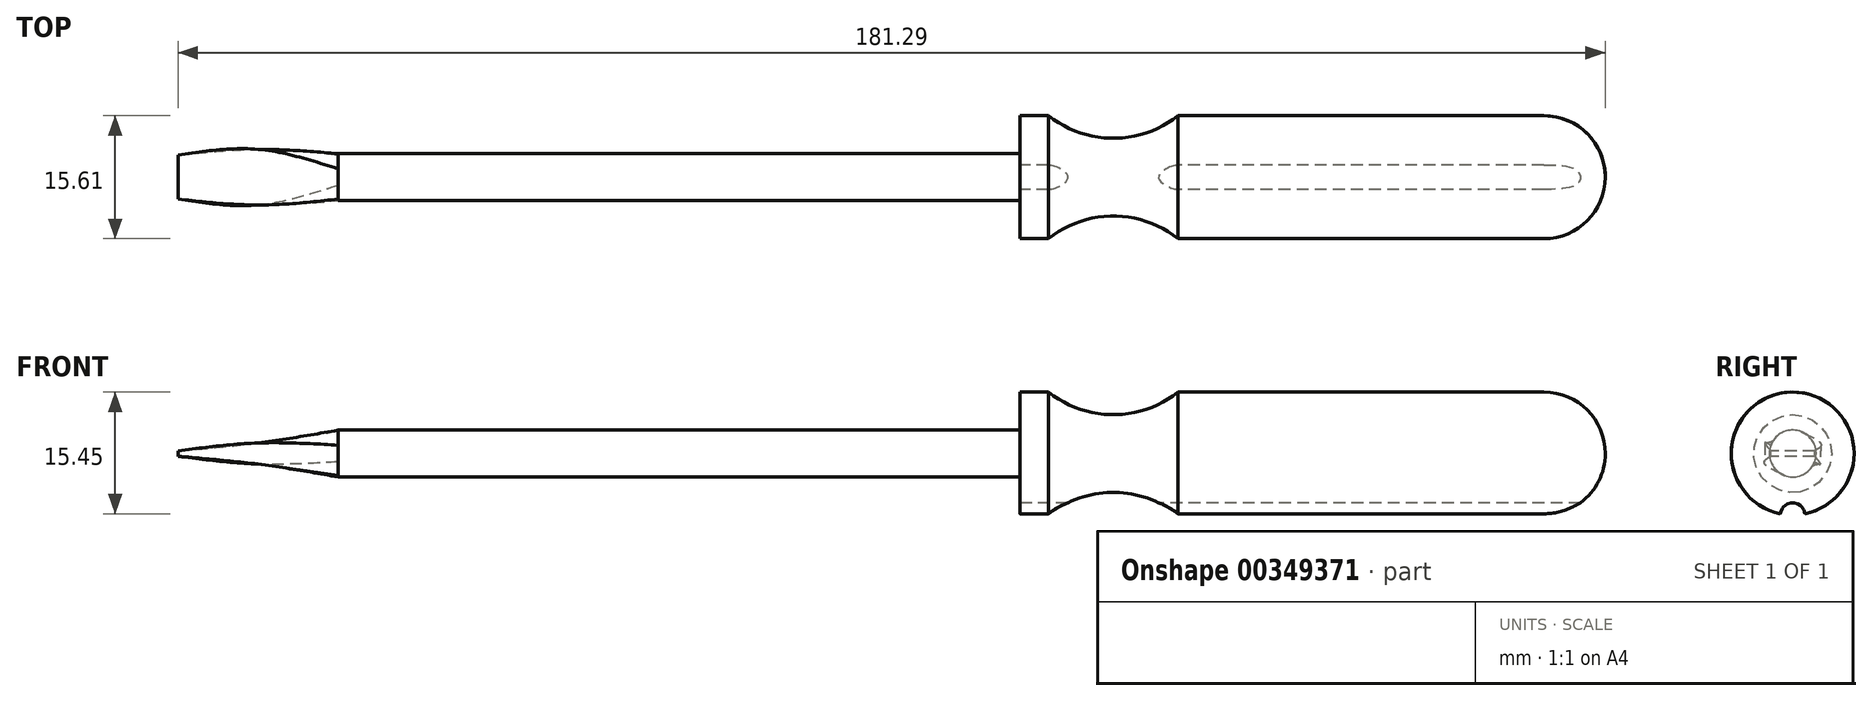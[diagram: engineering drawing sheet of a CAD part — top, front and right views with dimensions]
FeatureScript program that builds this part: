
annotation { "Feature Type Name" : "Feature", "Feature Type Description" : "" }
export const myFeature = defineFeature(function(context is Context, id is Id, definition is map)
    precondition{}
    {
        {
            var Q0;
            Q0=qCreatedBy(makeId("Top.planeOp"),FACE);
            var sketch = newSketch(context, id + "F0", { "sketchPlane" : qUnion([Q0])});
            skLineSegment(sketch, "E0", {"start": v(0, 0) * mm, "end": v(-46.47, 0) * mm});
            skLineSegment(sketch, "E1", {"start": v(0, 0) * mm, "end": v(0, -7.8) * mm, "construction": true});
            skArc(sketch, "E2", {"start": v(0, 0) * mm, "mid": v(5.52, -2.29) * mm, "end": v(7.8, -7.8) * mm});
            skLineSegment(sketch, "E3", {"start": v(7.8, -7.8) * mm, "end": v(-66.56, -7.8) * mm});
            skLineSegment(sketch, "E4", {"start": v(-66.56, -7.8) * mm, "end": v(-66.56, 0) * mm});
            skLineSegment(sketch, "E5", {"start": v(-66.56, 0) * mm, "end": v(-62.92, 0) * mm});
            skArc(sketch, "E6", {"start": v(-62.92, 0) * mm, "mid": v(-54.7, -2.86) * mm, "end": v(-46.47, 0) * mm});
            skSolve(sketch);
        }
        {
            var Q0;
            Q0=makeQuery(id+"F0.imprint","IMPRINT",FACE,{"disambiguationData":[TD([[makeQuery(id+"F0.imprint","IMPRINT",EDGE,{"derivedFrom":sQuery(id+"F0.wireOp",EDGE,"E0")}),1.0]])]});
            var Q1;
            Q1=sQuery(id+"F0.wireOp",EDGE,"E3");
            revolve(context, id + "F1", {"entities" : qUnion([Q0]), "axis" : qUnion([Q1]), "revolveType" : RevolveType.FULL});
        }
        {
            var Q0;
            Q0=makeQuery(id+"F1.opRevolve","SWEPT_FACE",FACE,{"disambiguationData":[OSD([sQuery(id+"F0.wireOp",EDGE,"E4")])]});
            var sketch = newSketch(context, id + "F2", { "sketchPlane" : qUnion([Q0])});
            skCircle(sketch, "E7.0", {"center": v(7.8, 0) * mm, "radius": 2.98 * mm});
            skSolve(sketch);
        }
        {
            var Q0;
            Q0=makeQuery(id+"F2.imprint","IMPRINT",FACE,{"disambiguationData":[TD([[makeQuery(id+"F2.imprint","IMPRINT",EDGE,{"derivedFrom":sQuery(id+"F2.wireOp",EDGE,"E7.0")}),1.0]])]});
            extrude(context, id + "F3", {"entities" : qUnion([Q0]), "operationType" : NewBodyOperationType.ADD, "depth" : 86.61 * mm});
        }
        {
            var Q0;
            Q0=makeQuery(id+"F3.opExtrude","CAP_FACE",FACE,{"disambiguationData":[OSD([sQuery(id+"F2.wireOp",EDGE,"E7.0")])],"isStart":false});
            cPlane(context, id + "F4", {"entities" : qUnion([Q0]), "cplaneType" : CPlaneType.OFFSET, "offset" : 10.16 * mm, "width" : 152.4 * mm, "height" : 152.4 * mm});
        }
        {
            var Q0;
            Q0=qCreatedBy(id+"F4.planeOp",FACE);
            cPlane(context, id + "F5", {"entities" : qUnion([Q0]), "cplaneType" : CPlaneType.OFFSET, "offset" : 10.16 * mm, "width" : 152.4 * mm, "height" : 152.4 * mm});
        }
        {
            var Q0;
            Q0=qCreatedBy(id+"F4.planeOp",FACE);
            var sketch = newSketch(context, id + "F6", { "sketchPlane" : qUnion([Q0])});
            skLineSegment(sketch, "E8.bottom", {"start": v(4.27, -1.34) * mm, "end": v(11.34, -1.34) * mm});
            skLineSegment(sketch, "E8.top", {"start": v(4.27, 1.34) * mm, "end": v(11.34, 1.34) * mm});
            skLineSegment(sketch, "E8.left", {"start": v(4.27, -1.34) * mm, "end": v(4.27, 1.34) * mm});
            skLineSegment(sketch, "E8.right", {"start": v(11.34, -1.34) * mm, "end": v(11.34, 1.34) * mm});
            skPoint(sketch, "E8.middle", {"position": v(7.8, 0) * mm});
            skSolve(sketch);
        }
        {
            var Q0;
            Q0=qCreatedBy(id+"F5.planeOp",FACE);
            var sketch = newSketch(context, id + "F7", { "sketchPlane" : qUnion([Q0])});
            skLineSegment(sketch, "E9.bottom", {"start": v(5, -0.35) * mm, "end": v(10.58, -0.35) * mm});
            skLineSegment(sketch, "E9.top", {"start": v(5, 0.35) * mm, "end": v(10.58, 0.35) * mm});
            skLineSegment(sketch, "E9.left", {"start": v(5, -0.35) * mm, "end": v(5, 0.35) * mm});
            skLineSegment(sketch, "E9.right", {"start": v(10.58, -0.35) * mm, "end": v(10.58, 0.35) * mm});
            skPoint(sketch, "E9.middle", {"position": v(7.79, 0) * mm});
            skSolve(sketch);
        }
        {
            var Q0;
            Q0=makeQuery(id+"F3.opExtrude","CAP_FACE",FACE,{"disambiguationData":[OSD([sQuery(id+"F2.wireOp",EDGE,"E7.0")])],"isStart":false});
            var Q1;
            Q1=makeQuery(id+"F6.imprint","IMPRINT",FACE,{"disambiguationData":[TD([[makeQuery(id+"F6.imprint","IMPRINT",EDGE,{"derivedFrom":sQuery(id+"F6.wireOp",EDGE,"E8.bottom")}),1.0]])]});
            var Q2;
            Q2=makeQuery(id+"F7.imprint","IMPRINT",FACE,{"disambiguationData":[TD([[makeQuery(id+"F7.imprint","IMPRINT",EDGE,{"derivedFrom":sQuery(id+"F7.wireOp",EDGE,"E9.bottom")}),1.0]])]});
            loft(context, id + "F8", {"sheetProfilesArray" : [{ "sheetProfileEntities" : qUnion([Q0]) }, { "sheetProfileEntities" : qUnion([Q1]) }, { "sheetProfileEntities" : qUnion([Q2]) }]});
        }
        {
            var Q0;
            Q0=makeQuery(id+"F1.opRevolve","SWEPT_FACE",FACE,{"disambiguationData":[OSD([sQuery(id+"F0.wireOp",EDGE,"E4")])]});
            var sketch = newSketch(context, id + "F9", { "sketchPlane" : qUnion([Q0])});
            skCircle(sketch, "E10", {"center": v(7.81, -7.8) * mm, "radius": 1.55 * mm});
            skSolve(sketch);
        }
        {
            var Q0;
            {var subQ0=sQuery(id+"F9.wireOp",EDGE,"E10");var subQ1=makeQuery(id+"F1.opRevolve","SWEPT_EDGE",EDGE,{"disambiguationData":[OSD([sQuery(id+"F0.wireOp",EDGE,"E4"),sQuery(id+"F0.wireOp",EDGE,"E5")])]});var subQ2=makeQuery(id+"F9.imprint","INTERSECT",VERTEX,{"disambiguationData":[OD(0.0)],"derivedFrom":[subQ1,subQ0]});Q0=makeQuery(id+"F9.imprint","IMPRINT",FACE,{"disambiguationData":[TD([[makeQuery(id+"F9.imprint","IMPRINT",EDGE,{"disambiguationData":[TD([[subQ2,-1.0]])],"derivedFrom":subQ0}),1.0]])]});}
            var Q1;
            Q1=sQuery(id+"F9.wireOp",EDGE,"E10");
            extrude(context, id + "F10", {"entities" : qUnion([Q0]), "operationType" : NewBodyOperationType.REMOVE, "surfaceEntities" : qUnion([Q1]), "oppositeDirection" : true, "depth" : 82.73 * mm});
        }
    });
